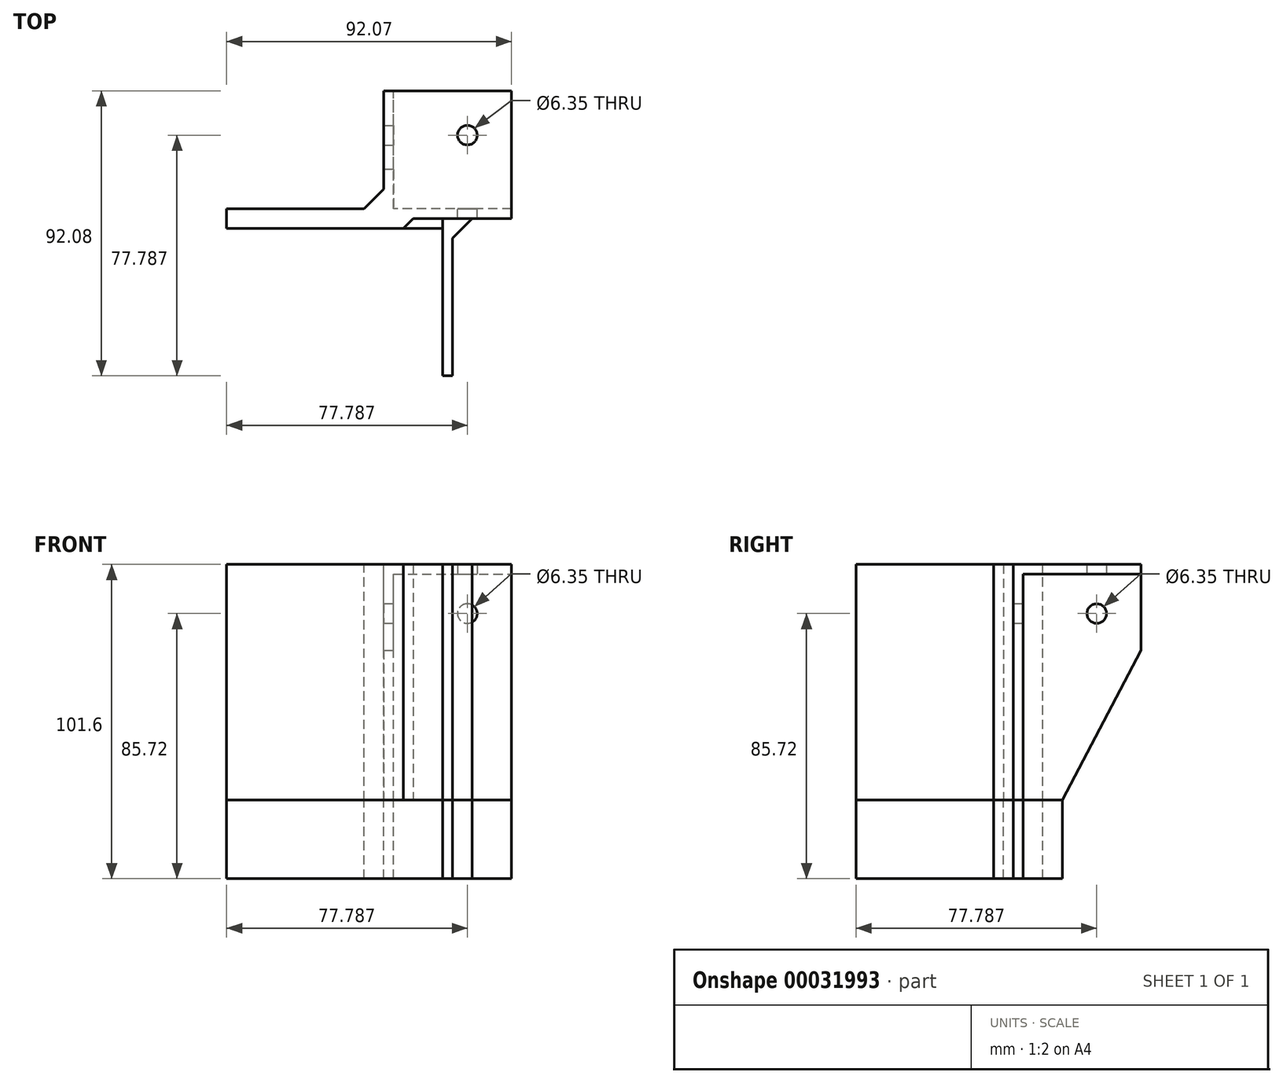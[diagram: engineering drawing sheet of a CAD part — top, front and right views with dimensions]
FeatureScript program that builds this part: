
annotation { "Feature Type Name" : "Feature", "Feature Type Description" : "" }
export const myFeature = defineFeature(function(context is Context, id is Id, definition is map)
    precondition{}
    {
        {
            var Q0;
            Q0=qCreatedBy(makeId("Top.planeOp"),FACE);
            var sketch = newSketch(context, id + "F0", { "sketchPlane" : qUnion([Q0])});
            skLineSegment(sketch, "E0.bottom", {"start": v(0, 0) * mm, "end": v(50.8, 0) * mm});
            skLineSegment(sketch, "E0.top", {"start": v(0, 50.8) * mm, "end": v(50.8, 50.8) * mm});
            skLineSegment(sketch, "E0.left", {"start": v(0, 0) * mm, "end": v(0, 50.8) * mm});
            skLineSegment(sketch, "E0.right", {"start": v(50.8, 0) * mm, "end": v(50.8, 50.8) * mm});
            skSolve(sketch);
        }
        {
            var Q0;
            Q0=makeQuery(id+"F0.imprint","IMPRINT",FACE,{"disambiguationData":[TD([[makeQuery(id+"F0.imprint","IMPRINT",EDGE,{"derivedFrom":sQuery(id+"F0.wireOp",EDGE,"E0.bottom")}),1.0]])]});
            extrude(context, id + "F1", {"entities" : qUnion([Q0]), "depth" : 3.17 * mm});
        }
        {
            var Q0;
            Q0=makeQuery(id+"F1.opExtrude","CAP_FACE",FACE,{"disambiguationData":[OSD([sQuery(id+"F0.wireOp",EDGE,"E0.bottom"),sQuery(id+"F0.wireOp",EDGE,"E0.top"),sQuery(id+"F0.wireOp",EDGE,"E0.left"),sQuery(id+"F0.wireOp",EDGE,"E0.right")])],"isStart":false});
            var sketch = newSketch(context, id + "F2", { "sketchPlane" : qUnion([Q0])});
            skLineSegment(sketch, "E1.bottom", {"start": v(50.8, 0) * mm, "end": v(-50.8, 0) * mm});
            skLineSegment(sketch, "E1.top", {"start": v(50.8, 3.18) * mm, "end": v(-50.8, 3.18) * mm});
            skLineSegment(sketch, "E1.left", {"start": v(50.8, 0) * mm, "end": v(50.8, 3.18) * mm});
            skLineSegment(sketch, "E1.right", {"start": v(-50.8, 0) * mm, "end": v(-50.8, 3.18) * mm});
            skSolve(sketch);
        }
        {
            var Q0;
            {var subQ5=sQuery(id+"F2.wireOp",EDGE,"E1.right");Q0=makeQuery(id+"F2.imprint","IMPRINT",FACE,{"disambiguationData":[TD([[makeQuery(id+"F2.imprint","IMPRINT",EDGE,{"derivedFrom":subQ5}),-1.0]])]});}
            var Q1;
            {var subQ5=sQuery(id+"F2.wireOp",EDGE,"E1.left");Q1=makeQuery(id+"F2.imprint","IMPRINT",FACE,{"disambiguationData":[TD([[makeQuery(id+"F2.imprint","IMPRINT",EDGE,{"derivedFrom":subQ5}),1.0]])]});}
            extrude(context, id + "F3", {"entities" : qUnion([Q0, Q1]), "operationType" : NewBodyOperationType.ADD, "depth" : 12.7 * mm, "hasSecondDirection" : true, "secondDirectionOppositeDirection" : true, "secondDirectionDepth" : 76.2 * mm});
        }
        {
            var Q0;
            Q0=makeQuery(id+"F1.opExtrude","CAP_FACE",FACE,{"disambiguationData":[OSD([sQuery(id+"F0.wireOp",EDGE,"E0.bottom"),sQuery(id+"F0.wireOp",EDGE,"E0.top"),sQuery(id+"F0.wireOp",EDGE,"E0.left"),sQuery(id+"F0.wireOp",EDGE,"E0.right")])],"isStart":false});
            var sketch = newSketch(context, id + "F4", { "sketchPlane" : qUnion([Q0])});
            skLineSegment(sketch, "E2.bottom", {"start": v(0, 50.8) * mm, "end": v(3.18, 50.8) * mm});
            skLineSegment(sketch, "E2.top", {"start": v(0, -50.8) * mm, "end": v(3.18, -50.8) * mm});
            skLineSegment(sketch, "E2.left", {"start": v(0, 50.8) * mm, "end": v(0, -50.8) * mm});
            skLineSegment(sketch, "E2.right", {"start": v(3.18, 50.8) * mm, "end": v(3.18, -50.8) * mm});
            skSolve(sketch);
        }
        {
            var Q0;
            Q0=qSketchRegion(id+"F4",true);
            extrude(context, id + "F5", {"entities" : qUnion([Q0]), "operationType" : NewBodyOperationType.ADD, "depth" : 12.7 * mm, "hasSecondDirection" : true, "secondDirectionOppositeDirection" : true, "secondDirectionDepth" : 76.2 * mm});
        }
        {
            var Q0;
            Q0=makeQuery(id+"F5.boolean.opBoolean","MERGE",FACE,{"derivedFrom":[makeQuery(id+"F3.opExtrude","CAP_FACE",FACE,{"disambiguationData":[OSD([sQuery(id+"F2.wireOp",EDGE,"E1.bottom"),sQuery(id+"F2.wireOp",EDGE,"E1.top"),sQuery(id+"F2.wireOp",EDGE,"E1.left"),sQuery(id+"F2.wireOp",EDGE,"E1.right")])],"isStart":false}),makeQuery(id+"F5.opExtrude","CAP_FACE",FACE,{"disambiguationData":[OSD([sQuery(id+"F4.wireOp",EDGE,"E2.bottom"),sQuery(id+"F4.wireOp",EDGE,"E2.top"),sQuery(id+"F4.wireOp",EDGE,"E2.left"),sQuery(id+"F4.wireOp",EDGE,"E2.right")])],"isStart":false})]});
            var sketch = newSketch(context, id + "F6", { "sketchPlane" : qUnion([Q0])});
            skLineSegment(sketch, "E3.0", {"start": v(3.18, 50.8) * mm, "end": v(3.18, 3.18) * mm});
            skLineSegment(sketch, "E3.1", {"start": v(0, 50.8) * mm, "end": v(3.18, 50.8) * mm});
            skLineSegment(sketch, "E3.2", {"start": v(0, 50.8) * mm, "end": v(0, 3.18) * mm});
            skLineSegment(sketch, "E3.3", {"start": v(50.8, 3.18) * mm, "end": v(3.18, 3.18) * mm});
            skLineSegment(sketch, "E3.4", {"start": v(50.8, 0) * mm, "end": v(3.18, 0) * mm});
            skLineSegment(sketch, "E3.5", {"start": v(50.8, 0) * mm, "end": v(50.8, 3.18) * mm});
            skLineSegment(sketch, "E4", {"start": v(3.18, 0) * mm, "end": v(0, 0) * mm});
            skLineSegment(sketch, "E5", {"start": v(0, 0) * mm, "end": v(0, 3.18) * mm});
            skSolve(sketch);
        }
        {
            var Q0;
            {var subQ0=sQuery(id+"F4.wireOp",EDGE,"E2.right");var subQ3=sQuery(id+"F0.wireOp",EDGE,"E0.top");Q0=makeQuery(id+"F5.boolean.opBoolean","SPLIT",FACE,{"disambiguationData":[TD([makeQuery(id+"F1.opExtrude","CAP_FACE",FACE,{"disambiguationData":[OSD([sQuery(id+"F0.wireOp",EDGE,"E0.bottom"),subQ3,sQuery(id+"F0.wireOp",EDGE,"E0.left"),sQuery(id+"F0.wireOp",EDGE,"E0.right")])],"isStart":false})])],"derivedFrom":makeQuery(id+"F5.opExtrude","SWEPT_FACE",FACE,{"disambiguationData":[OSD([subQ0])]})});}
            var sketch = newSketch(context, id + "F7", { "sketchPlane" : qUnion([Q0])});
            skLineSegment(sketch, "E6.0", {"start": v(50.8, 15.88) * mm, "end": v(50.8, 3.18) * mm});
            skLineSegment(sketch, "E6.1", {"start": v(3.18, 3.18) * mm, "end": v(50.8, 3.18) * mm});
            skLineSegment(sketch, "E6.2", {"start": v(50.8, 15.88) * mm, "end": v(3.18, 15.88) * mm});
            skLineSegment(sketch, "E6.3", {"start": v(3.18, 3.18) * mm, "end": v(3.18, 15.88) * mm});
            skSolve(sketch);
        }
        {
            var Q0;
            Q0=makeQuery(id+"F7.imprint","IMPRINT",FACE,{"disambiguationData":[TD([[makeQuery(id+"F7.imprint","IMPRINT",EDGE,{"derivedFrom":sQuery(id+"F7.wireOp",EDGE,"E6.0")}),-1.0]])]});
            extrude(context, id + "F8", {"entities" : qUnion([Q0]), "operationType" : NewBodyOperationType.REMOVE, "oppositeDirection" : true, "depth" : 25.4 * mm});
        }
        {
            var Q0;
            {var subQ0=sQuery(id+"F2.wireOp",EDGE,"E1.top");var subQ1=makeQuery(id+"F3.opExtrude","SWEPT_FACE",FACE,{"disambiguationData":[OSD([subQ0])]});var subQ11=sQuery(id+"F0.wireOp",EDGE,"E0.left");var subQ12=sQuery(id+"F0.wireOp",EDGE,"E0.right");Q0=makeQuery(id+"F8.boolean.opBoolean","MERGE",FACE,{"derivedFrom":[makeQuery(id+"F5.boolean.opBoolean","SPLIT",FACE,{"disambiguationData":[TD([makeQuery(id+"F1.opExtrude","SWEPT_FACE",FACE,{"disambiguationData":[OSD([subQ11])]})])],"derivedFrom":subQ1}),makeQuery(id+"F5.boolean.opBoolean","SPLIT",FACE,{"disambiguationData":[TD([makeQuery(id+"F1.opExtrude","CAP_FACE",FACE,{"disambiguationData":[OSD([sQuery(id+"F0.wireOp",EDGE,"E0.bottom"),sQuery(id+"F0.wireOp",EDGE,"E0.top"),subQ11,subQ12])],"isStart":false})])],"derivedFrom":subQ1}),makeQuery(id+"F8.opExtrude","SWEPT_FACE",FACE,{"disambiguationData":[OSD([sQuery(id+"F7.wireOp",EDGE,"E6.3")])]})]});}
            var sketch = newSketch(context, id + "F9", { "sketchPlane" : qUnion([Q0])});
            skLineSegment(sketch, "E7.0", {"start": v(-50.8, 15.88) * mm, "end": v(-3.18, 15.88) * mm});
            skLineSegment(sketch, "E7.1", {"start": v(-3.18, 3.18) * mm, "end": v(-50.8, 3.18) * mm});
            skLineSegment(sketch, "E7.2", {"start": v(-50.8, 15.88) * mm, "end": v(-50.8, 3.18) * mm});
            skLineSegment(sketch, "E8", {"start": v(-3.18, 15.88) * mm, "end": v(-3.18, 3.18) * mm});
            skPoint(sketch, "E9.orphan", {"position": v(0, 3.18) * mm});
            skSolve(sketch);
        }
        {
            var Q0;
            Q0=makeQuery(id+"F9.imprint","IMPRINT",FACE,{"disambiguationData":[TD([[makeQuery(id+"F9.imprint","IMPRINT",EDGE,{"derivedFrom":sQuery(id+"F9.wireOp",EDGE,"E7.0")}),-1.0]])]});
            extrude(context, id + "F10", {"entities" : qUnion([Q0]), "operationType" : NewBodyOperationType.REMOVE, "oppositeDirection" : true, "depth" : 25.4 * mm});
        }
        {
            var Q0;
            {var subQ0=sQuery(id+"F2.wireOp",EDGE,"E1.bottom");Q0=makeQuery(id+"F5.boolean.opBoolean","SPLIT",FACE,{"disambiguationData":[TD([makeQuery(id+"F1.opExtrude","SWEPT_FACE",FACE,{"disambiguationData":[OSD([sQuery(id+"F0.wireOp",EDGE,"E0.right")])]})])],"derivedFrom":makeQuery(id+"F3.boolean.opBoolean","MERGE",FACE,{"derivedFrom":[makeQuery(id+"F1.opExtrude","SWEPT_FACE",FACE,{"disambiguationData":[OSD([sQuery(id+"F0.wireOp",EDGE,"E0.bottom")])]}),makeQuery(id+"F3.opExtrude","SWEPT_FACE",FACE,{"disambiguationData":[OSD([subQ0])]})]})});}
            var sketch = newSketch(context, id + "F11", { "sketchPlane" : qUnion([Q0])});
            skLineSegment(sketch, "E10", {"start": v(3.18, -73.03) * mm, "end": v(41.28, -73.03) * mm, "construction": true});
            skLineSegment(sketch, "E11", {"start": v(50.8, 0) * mm, "end": v(50.8, -6.35) * mm, "construction": true});
            skLineSegment(sketch, "E12", {"start": v(41.28, -73.03) * mm, "end": v(50.8, -6.35) * mm});
            skLineSegment(sketch, "E13", {"start": v(50.8, -6.35) * mm, "end": v(50.8, -73.03) * mm});
            skLineSegment(sketch, "E14", {"start": v(50.8, -73.03) * mm, "end": v(41.28, -73.03) * mm});
            skSolve(sketch);
        }
        {
            var Q0;
            Q0=makeQuery(id+"F11.imprint","IMPRINT",FACE,{"disambiguationData":[TD([[makeQuery(id+"F11.imprint","IMPRINT",EDGE,{"derivedFrom":sQuery(id+"F11.wireOp",EDGE,"E12")}),-1.0]])]});
            extrude(context, id + "F12", {"entities" : qUnion([Q0]), "operationType" : NewBodyOperationType.REMOVE, "oppositeDirection" : true, "depth" : 25.4 * mm});
        }
        {
            var Q0;
            Q0=makeQuery(id+"F5.boolean.opBoolean","MERGE",FACE,{"derivedFrom":[makeQuery(id+"F1.opExtrude","SWEPT_FACE",FACE,{"disambiguationData":[OSD([sQuery(id+"F0.wireOp",EDGE,"E0.left")])]}),makeQuery(id+"F5.opExtrude","SWEPT_FACE",FACE,{"disambiguationData":[OSD([sQuery(id+"F4.wireOp",EDGE,"E2.left")])]})]});
            var sketch = newSketch(context, id + "F13", { "sketchPlane" : qUnion([Q0])});
            skLineSegment(sketch, "E15", {"start": v(-50.8, 3.18) * mm, "end": v(-50.8, -6.35) * mm, "construction": true});
            skLineSegment(sketch, "E16", {"start": v(-50.8, -6.35) * mm, "end": v(-15.88, -73.03) * mm});
            skLineSegment(sketch, "E17", {"start": v(-15.88, -73.03) * mm, "end": v(-3.18, -73.03) * mm, "construction": true});
            skLineSegment(sketch, "E18", {"start": v(-50.8, -6.35) * mm, "end": v(-50.8, -73.03) * mm});
            skLineSegment(sketch, "E19", {"start": v(-50.8, -73.03) * mm, "end": v(-15.88, -73.03) * mm});
            skSolve(sketch);
        }
        {
            var Q0;
            Q0=makeQuery(id+"F13.imprint","IMPRINT",FACE,{"disambiguationData":[TD([[makeQuery(id+"F13.imprint","IMPRINT",EDGE,{"derivedFrom":sQuery(id+"F13.wireOp",EDGE,"E16")}),-1.0]])]});
            extrude(context, id + "F14", {"entities" : qUnion([Q0]), "operationType" : NewBodyOperationType.REMOVE, "oppositeDirection" : true, "depth" : 25.4 * mm});
        }
        {
            var Q0;
            {var subQ0=sQuery(id+"F2.wireOp",EDGE,"E1.top");var subQ1=makeQuery(id+"F3.opExtrude","SWEPT_FACE",FACE,{"disambiguationData":[OSD([subQ0])]});var subQ11=sQuery(id+"F0.wireOp",EDGE,"E0.left");var subQ12=sQuery(id+"F0.wireOp",EDGE,"E0.right");Q0=makeQuery(id+"F8.boolean.opBoolean","MERGE",FACE,{"derivedFrom":[makeQuery(id+"F5.boolean.opBoolean","SPLIT",FACE,{"disambiguationData":[TD([makeQuery(id+"F1.opExtrude","SWEPT_FACE",FACE,{"disambiguationData":[OSD([subQ11])]})])],"derivedFrom":subQ1}),makeQuery(id+"F5.boolean.opBoolean","SPLIT",FACE,{"disambiguationData":[TD([makeQuery(id+"F1.opExtrude","CAP_FACE",FACE,{"disambiguationData":[OSD([sQuery(id+"F0.wireOp",EDGE,"E0.bottom"),sQuery(id+"F0.wireOp",EDGE,"E0.top"),subQ11,subQ12])],"isStart":false})])],"derivedFrom":subQ1}),makeQuery(id+"F8.opExtrude","SWEPT_FACE",FACE,{"disambiguationData":[OSD([sQuery(id+"F7.wireOp",EDGE,"E6.3")])]})]});}
            var sketch = newSketch(context, id + "F15", { "sketchPlane" : qUnion([Q0])});
            skLineSegment(sketch, "E20.bottom", {"start": v(-3.18, 15.88) * mm, "end": v(50.8, 15.88) * mm});
            skLineSegment(sketch, "E20.top", {"start": v(-3.18, 3.18) * mm, "end": v(50.8, 3.18) * mm});
            skLineSegment(sketch, "E20.left", {"start": v(-3.18, 15.88) * mm, "end": v(-3.18, 3.18) * mm});
            skLineSegment(sketch, "E20.right", {"start": v(50.8, 15.88) * mm, "end": v(50.8, 3.18) * mm});
            skSolve(sketch);
        }
        {
            var Q0;
            Q0=makeQuery(id+"F15.imprint","IMPRINT",FACE,{"disambiguationData":[TD([[makeQuery(id+"F15.imprint","IMPRINT",EDGE,{"derivedFrom":sQuery(id+"F15.wireOp",EDGE,"E20.bottom")}),-1.0]])]});
            extrude(context, id + "F16", {"entities" : qUnion([Q0]), "operationType" : NewBodyOperationType.REMOVE, "endBound" : BoundingType.THROUGH_ALL, "oppositeDirection" : true, "depth" : 25.4 * mm});
        }
        {
            var Q0;
            Q0=makeQuery(id+"F16.boolean.opBoolean","MERGE",FACE,{"derivedFrom":[makeQuery(id+"F10.boolean.opBoolean","MERGE",FACE,{"derivedFrom":[makeQuery(id+"F8.boolean.opBoolean","MERGE",FACE,{"derivedFrom":[makeQuery(id+"F1.opExtrude","CAP_FACE",FACE,{"disambiguationData":[OSD([sQuery(id+"F0.wireOp",EDGE,"E0.bottom"),sQuery(id+"F0.wireOp",EDGE,"E0.top"),sQuery(id+"F0.wireOp",EDGE,"E0.left"),sQuery(id+"F0.wireOp",EDGE,"E0.right")])],"isStart":false}),makeQuery(id+"F8.opExtrude","SWEPT_FACE",FACE,{"disambiguationData":[OSD([sQuery(id+"F7.wireOp",EDGE,"E6.1")])]})]}),makeQuery(id+"F10.opExtrude","SWEPT_FACE",FACE,{"disambiguationData":[OSD([sQuery(id+"F9.wireOp",EDGE,"E7.1")])]})]}),makeQuery(id+"F16.opExtrude","SWEPT_FACE",FACE,{"disambiguationData":[OSD([sQuery(id+"F15.wireOp",EDGE,"E20.top")])]})]});
            var sketch = newSketch(context, id + "F17", { "sketchPlane" : qUnion([Q0])});
            skLineSegment(sketch, "E21", {"start": v(3.18, 0) * mm, "end": v(3.18, -6.35) * mm});
            skLineSegment(sketch, "E22", {"start": v(3.18, -6.35) * mm, "end": v(9.53, 0) * mm});
            skLineSegment(sketch, "E23", {"start": v(9.53, 0) * mm, "end": v(3.18, 0) * mm});
            skLineSegment(sketch, "E24", {"start": v(0, 3.18) * mm, "end": v(0, 9.53) * mm});
            skLineSegment(sketch, "E25", {"start": v(0, 9.53) * mm, "end": v(-6.35, 3.18) * mm});
            skLineSegment(sketch, "E26", {"start": v(-6.35, 3.18) * mm, "end": v(0, 3.18) * mm});
            skSolve(sketch);
        }
        {
            var Q0;
            Q0=qSketchRegion(id+"F17",true);
            var Q1;
            Q1=makeQuery(id+"F5.boolean.opBoolean","MERGE",FACE,{"derivedFrom":[makeQuery(id+"F3.opExtrude","CAP_FACE",FACE,{"disambiguationData":[OSD([sQuery(id+"F2.wireOp",EDGE,"E1.bottom"),sQuery(id+"F2.wireOp",EDGE,"E1.top"),sQuery(id+"F2.wireOp",EDGE,"E1.left"),sQuery(id+"F2.wireOp",EDGE,"E1.right")])],"isStart":true}),makeQuery(id+"F5.opExtrude","CAP_FACE",FACE,{"disambiguationData":[OSD([sQuery(id+"F4.wireOp",EDGE,"E2.bottom"),sQuery(id+"F4.wireOp",EDGE,"E2.top"),sQuery(id+"F4.wireOp",EDGE,"E2.left"),sQuery(id+"F4.wireOp",EDGE,"E2.right")])],"isStart":true})]});
            extrude(context, id + "F18", {"entities" : qUnion([Q0]), "operationType" : NewBodyOperationType.ADD, "endBound" : BoundingType.UP_TO_SURFACE, "oppositeDirection" : true, "endBoundEntityFace" : qUnion([Q1]), "depth" : 25.4 * mm});
        }
        {
            var Q0;
            {var subQ0=sQuery(id+"F2.wireOp",EDGE,"E1.top");var subQ3=sQuery(id+"F0.wireOp",EDGE,"E0.right");Q0=makeQuery(id+"F5.boolean.opBoolean","SPLIT",FACE,{"disambiguationData":[TD([makeQuery(id+"F1.opExtrude","CAP_FACE",FACE,{"disambiguationData":[OSD([sQuery(id+"F0.wireOp",EDGE,"E0.bottom"),sQuery(id+"F0.wireOp",EDGE,"E0.top"),sQuery(id+"F0.wireOp",EDGE,"E0.left"),subQ3])],"isStart":true})])],"derivedFrom":makeQuery(id+"F3.opExtrude","SWEPT_FACE",FACE,{"disambiguationData":[OSD([subQ0])]})});}
            var sketch = newSketch(context, id + "F19", { "sketchPlane" : qUnion([Q0])});
            skLineSegment(sketch, "E27", {"start": v(-26.99, 0) * mm, "end": v(-26.99, -12.7) * mm, "construction": true});
            skPoint(sketch, "E27.endSnap0", {"position": v(-26.99, 0) * mm});
            skCircle(sketch, "E28", {"center": v(-26.99, -12.7) * mm, "radius": 3.18 * mm});
            skSolve(sketch);
        }
        {
            var Q0;
            Q0=qSketchRegion(id+"F19",true);
            extrude(context, id + "F20", {"entities" : qUnion([Q0]), "operationType" : NewBodyOperationType.REMOVE, "oppositeDirection" : true, "depth" : 25.4 * mm});
        }
        {
            var Q0;
            {var subQ0=sQuery(id+"F4.wireOp",EDGE,"E2.right");var subQ3=sQuery(id+"F0.wireOp",EDGE,"E0.top");Q0=makeQuery(id+"F5.boolean.opBoolean","SPLIT",FACE,{"disambiguationData":[TD([makeQuery(id+"F1.opExtrude","CAP_FACE",FACE,{"disambiguationData":[OSD([sQuery(id+"F0.wireOp",EDGE,"E0.bottom"),subQ3,sQuery(id+"F0.wireOp",EDGE,"E0.left"),sQuery(id+"F0.wireOp",EDGE,"E0.right")])],"isStart":true})])],"derivedFrom":makeQuery(id+"F5.opExtrude","SWEPT_FACE",FACE,{"disambiguationData":[OSD([subQ0])]})});}
            var sketch = newSketch(context, id + "F21", { "sketchPlane" : qUnion([Q0])});
            skLineSegment(sketch, "E29", {"start": v(26.99, 0) * mm, "end": v(26.99, -12.7) * mm, "construction": true});
            skPoint(sketch, "E29.endSnap0", {"position": v(26.99, 0) * mm});
            skCircle(sketch, "E30", {"center": v(26.99, -12.7) * mm, "radius": 3.18 * mm});
            skSolve(sketch);
        }
        {
            var Q0;
            Q0=makeQuery(id+"F21.imprint","IMPRINT",FACE,{"disambiguationData":[TD([[makeQuery(id+"F21.imprint","IMPRINT",EDGE,{"derivedFrom":sQuery(id+"F21.wireOp",EDGE,"E30")}),1.0]])]});
            extrude(context, id + "F22", {"entities" : qUnion([Q0]), "operationType" : NewBodyOperationType.REMOVE, "oppositeDirection" : true, "depth" : 25.4 * mm});
        }
        {
            var Q0;
            Q0=makeQuery(id+"F1.opExtrude","CAP_FACE",FACE,{"disambiguationData":[OSD([sQuery(id+"F0.wireOp",EDGE,"E0.bottom"),sQuery(id+"F0.wireOp",EDGE,"E0.top"),sQuery(id+"F0.wireOp",EDGE,"E0.left"),sQuery(id+"F0.wireOp",EDGE,"E0.right")])],"isStart":true});
            var sketch = newSketch(context, id + "F23", { "sketchPlane" : qUnion([Q0])});
            skLineSegment(sketch, "E31", {"start": v(3.18, -3.18) * mm, "end": v(50.8, -50.8) * mm, "construction": true});
            skLineSegment(sketch, "E32", {"start": v(50.8, -50.8) * mm, "end": v(50.8, -3.18) * mm, "construction": true});
            skLineSegment(sketch, "E33", {"start": v(50.8, -3.18) * mm, "end": v(3.17, -50.8) * mm, "construction": true});
            skCircle(sketch, "E34", {"center": v(26.99, -26.99) * mm, "radius": 3.18 * mm});
            skPoint(sketch, "E34.centerSnap0", {"position": v(26.99, -26.99) * mm});
            skSolve(sketch);
        }
        {
            var Q0;
            Q0=makeQuery(id+"F23.imprint","IMPRINT",FACE,{"disambiguationData":[TD([[makeQuery(id+"F23.imprint","IMPRINT",EDGE,{"derivedFrom":sQuery(id+"F23.wireOp",EDGE,"E34")}),1.0]])]});
            var Q1;
            Q1=sQuery(id+"F23.wireOp",EDGE,"E34");
            extrude(context, id + "F24", {"entities" : qUnion([Q0]), "operationType" : NewBodyOperationType.REMOVE, "surfaceEntities" : qUnion([Q1]), "oppositeDirection" : true, "depth" : 25.4 * mm});
        }
        {
            var Q0;
            Q0=makeQuery(id+"F18.boolean.opBoolean","MERGE",FACE,{"derivedFrom":[makeQuery(id+"F16.boolean.opBoolean","MERGE",FACE,{"derivedFrom":[makeQuery(id+"F10.boolean.opBoolean","MERGE",FACE,{"derivedFrom":[makeQuery(id+"F8.boolean.opBoolean","MERGE",FACE,{"derivedFrom":[makeQuery(id+"F1.opExtrude","CAP_FACE",FACE,{"disambiguationData":[OSD([sQuery(id+"F0.wireOp",EDGE,"E0.bottom"),sQuery(id+"F0.wireOp",EDGE,"E0.top"),sQuery(id+"F0.wireOp",EDGE,"E0.left"),sQuery(id+"F0.wireOp",EDGE,"E0.right")])],"isStart":false}),makeQuery(id+"F8.opExtrude","SWEPT_FACE",FACE,{"disambiguationData":[OSD([sQuery(id+"F7.wireOp",EDGE,"E6.1")])]})]}),makeQuery(id+"F10.opExtrude","SWEPT_FACE",FACE,{"disambiguationData":[OSD([sQuery(id+"F9.wireOp",EDGE,"E7.1")])]})]}),makeQuery(id+"F16.opExtrude","SWEPT_FACE",FACE,{"disambiguationData":[OSD([sQuery(id+"F15.wireOp",EDGE,"E20.top")])]})]}),makeQuery(id+"F18.opExtrude","CAP_FACE",FACE,{"disambiguationData":[OSD([sQuery(id+"F17.wireOp",EDGE,"E21"),sQuery(id+"F17.wireOp",EDGE,"E22"),sQuery(id+"F17.wireOp",EDGE,"E23")])],"isStart":true}),makeQuery(id+"F18.opExtrude","CAP_FACE",FACE,{"disambiguationData":[OSD([sQuery(id+"F17.wireOp",EDGE,"E24"),sQuery(id+"F17.wireOp",EDGE,"E25"),sQuery(id+"F17.wireOp",EDGE,"E26")])],"isStart":true})]});
            var sketch = newSketch(context, id + "F25", { "sketchPlane" : qUnion([Q0])});
            skLineSegment(sketch, "E35.bottom", {"start": v(50.8, 0) * mm, "end": v(41.28, 0) * mm});
            skLineSegment(sketch, "E35.top", {"start": v(50.8, 50.8) * mm, "end": v(41.27, 50.8) * mm});
            skLineSegment(sketch, "E35.left", {"start": v(50.8, 0) * mm, "end": v(50.8, 50.8) * mm});
            skLineSegment(sketch, "E35.right", {"start": v(41.28, 0) * mm, "end": v(41.27, 41.28) * mm});
            skLineSegment(sketch, "E36.bottom", {"start": v(41.27, 50.8) * mm, "end": v(0, 50.8) * mm});
            skLineSegment(sketch, "E36.top", {"start": v(41.27, 41.28) * mm, "end": v(0, 41.28) * mm});
            skLineSegment(sketch, "E36.right", {"start": v(0, 50.8) * mm, "end": v(0, 41.28) * mm});
            skSolve(sketch);
        }
        {
            var Q0;
            Q0=makeQuery(id+"F25.imprint","IMPRINT",FACE,{"disambiguationData":[TD([[makeQuery(id+"F25.imprint","IMPRINT",EDGE,{"derivedFrom":sQuery(id+"F25.wireOp",EDGE,"E35.bottom")}),1.0]])]});
            extrude(context, id + "F26", {"entities" : qUnion([Q0]), "operationType" : NewBodyOperationType.REMOVE, "endBound" : BoundingType.THROUGH_ALL, "oppositeDirection" : true, "depth" : 25.4 * mm});
        }
        {
            var Q0;
            {var subQ0=sQuery(id+"F2.wireOp",EDGE,"E1.bottom");var subQ5=sQuery(id+"F2.wireOp",EDGE,"E1.right");Q0=makeQuery(id+"F5.boolean.opBoolean","SPLIT",FACE,{"disambiguationData":[TD([makeQuery(id+"F3.opExtrude","SWEPT_FACE",FACE,{"disambiguationData":[OSD([subQ5])]})])],"derivedFrom":makeQuery(id+"F3.boolean.opBoolean","MERGE",FACE,{"derivedFrom":[makeQuery(id+"F1.opExtrude","SWEPT_FACE",FACE,{"disambiguationData":[OSD([sQuery(id+"F0.wireOp",EDGE,"E0.bottom")])]}),makeQuery(id+"F3.opExtrude","SWEPT_FACE",FACE,{"disambiguationData":[OSD([subQ0])]})]})});}
            extrude(context, id + "F27", {"entities" : qUnion([Q0]), "operationType" : NewBodyOperationType.ADD, "depth" : 3.17 * mm});
        }
        {
            var Q0;
            {var subQ0=sQuery(id+"F0.wireOp",EDGE,"E0.bottom");var subQ1=sQuery(id+"F15.wireOp",EDGE,"E20.top");Q0=makeQuery(id+"F27.boolean.opBoolean","MERGE",FACE,{"derivedFrom":[makeQuery(id+"F18.boolean.opBoolean","MERGE",FACE,{"derivedFrom":[makeQuery(id+"F16.boolean.opBoolean","MERGE",FACE,{"derivedFrom":[makeQuery(id+"F10.boolean.opBoolean","MERGE",FACE,{"derivedFrom":[makeQuery(id+"F8.boolean.opBoolean","MERGE",FACE,{"derivedFrom":[makeQuery(id+"F1.opExtrude","CAP_FACE",FACE,{"disambiguationData":[OSD([subQ0,sQuery(id+"F0.wireOp",EDGE,"E0.top"),sQuery(id+"F0.wireOp",EDGE,"E0.left"),sQuery(id+"F0.wireOp",EDGE,"E0.right")])],"isStart":false}),makeQuery(id+"F8.opExtrude","SWEPT_FACE",FACE,{"disambiguationData":[OSD([sQuery(id+"F7.wireOp",EDGE,"E6.1")])]})]}),makeQuery(id+"F10.opExtrude","SWEPT_FACE",FACE,{"disambiguationData":[OSD([sQuery(id+"F9.wireOp",EDGE,"E7.1")])]})]}),makeQuery(id+"F16.opExtrude","SWEPT_FACE",FACE,{"disambiguationData":[OSD([subQ1])]})]}),makeQuery(id+"F18.opExtrude","CAP_FACE",FACE,{"disambiguationData":[OSD([sQuery(id+"F17.wireOp",EDGE,"E21"),sQuery(id+"F17.wireOp",EDGE,"E22"),sQuery(id+"F17.wireOp",EDGE,"E23")])],"isStart":true}),makeQuery(id+"F18.opExtrude","CAP_FACE",FACE,{"disambiguationData":[OSD([sQuery(id+"F17.wireOp",EDGE,"E24"),sQuery(id+"F17.wireOp",EDGE,"E25"),sQuery(id+"F17.wireOp",EDGE,"E26")])],"isStart":true})]}),makeQuery(id+"F27.opExtrude","SWEPT_FACE",FACE,{"disambiguationData":[OSD([subQ0,sQuery(id+"F2.wireOp",EDGE,"E1.bottom"),subQ1])]})]});}
            var sketch = newSketch(context, id + "F28", { "sketchPlane" : qUnion([Q0])});
            skLineSegment(sketch, "E37", {"start": v(3.18, -12.1) * mm, "end": v(22.23, -12.1) * mm, "construction": true});
            skPoint(sketch, "E38.oppositeSnap0", {"position": v(1.59, -50.8) * mm});
            skLineSegment(sketch, "E38.bottom", {"start": v(22.23, 0) * mm, "end": v(19.05, 0) * mm});
            skLineSegment(sketch, "E38.top", {"start": v(22.23, -50.8) * mm, "end": v(19.05, -50.8) * mm});
            skLineSegment(sketch, "E38.left", {"start": v(22.23, -6.35) * mm, "end": v(22.23, -50.8) * mm});
            skLineSegment(sketch, "E38.right", {"start": v(19.05, 0) * mm, "end": v(19.05, -50.8) * mm});
            skLineSegment(sketch, "E39", {"start": v(22.23, 0) * mm, "end": v(28.57, 0) * mm});
            skLineSegment(sketch, "E40", {"start": v(28.57, 0) * mm, "end": v(22.23, -6.35) * mm});
            skSolve(sketch);
        }
        {
            var Q0;
            Q0=makeQuery(id+"F28.imprint","IMPRINT",FACE,{"disambiguationData":[TD([[makeQuery(id+"F28.imprint","IMPRINT",EDGE,{"derivedFrom":sQuery(id+"F28.wireOp",EDGE,"E38.bottom")}),-1.0]])]});
            var Q1;
            {var subQ0=sQuery(id+"F2.wireOp",EDGE,"E1.bottom");Q1=makeQuery(id+"F27.boolean.opBoolean","MERGE",FACE,{"derivedFrom":[makeQuery(id+"F18.boolean.opBoolean","MERGE",FACE,{"derivedFrom":[makeQuery(id+"F5.boolean.opBoolean","MERGE",FACE,{"derivedFrom":[makeQuery(id+"F3.opExtrude","CAP_FACE",FACE,{"disambiguationData":[OSD([subQ0,sQuery(id+"F2.wireOp",EDGE,"E1.top"),sQuery(id+"F2.wireOp",EDGE,"E1.left"),sQuery(id+"F2.wireOp",EDGE,"E1.right")])],"isStart":true}),makeQuery(id+"F5.opExtrude","CAP_FACE",FACE,{"disambiguationData":[OSD([sQuery(id+"F4.wireOp",EDGE,"E2.bottom"),sQuery(id+"F4.wireOp",EDGE,"E2.top"),sQuery(id+"F4.wireOp",EDGE,"E2.left"),sQuery(id+"F4.wireOp",EDGE,"E2.right")])],"isStart":true})]}),makeQuery(id+"F18.opExtrude","CAP_FACE",FACE,{"disambiguationData":[OSD([sQuery(id+"F17.wireOp",EDGE,"E21"),sQuery(id+"F17.wireOp",EDGE,"E22"),sQuery(id+"F17.wireOp",EDGE,"E23")])],"isStart":false}),makeQuery(id+"F18.opExtrude","CAP_FACE",FACE,{"disambiguationData":[OSD([sQuery(id+"F17.wireOp",EDGE,"E24"),sQuery(id+"F17.wireOp",EDGE,"E25"),sQuery(id+"F17.wireOp",EDGE,"E26")])],"isStart":false})]}),makeQuery(id+"F27.opExtrude","SWEPT_FACE",FACE,{"disambiguationData":[OSD([subQ0])]})]});}
            extrude(context, id + "F29", {"entities" : qUnion([Q0]), "endBound" : BoundingType.UP_TO_SURFACE, "oppositeDirection" : true, "endBoundEntityFace" : qUnion([Q1]), "depth" : 25.4 * mm});
        }
        {
            var Q0;
            {var subQ0=sQuery(id+"F0.wireOp",EDGE,"E0.bottom");var subQ1=sQuery(id+"F15.wireOp",EDGE,"E20.top");Q0=makeQuery(id+"F27.boolean.opBoolean","MERGE",FACE,{"derivedFrom":[makeQuery(id+"F18.boolean.opBoolean","MERGE",FACE,{"derivedFrom":[makeQuery(id+"F16.boolean.opBoolean","MERGE",FACE,{"derivedFrom":[makeQuery(id+"F10.boolean.opBoolean","MERGE",FACE,{"derivedFrom":[makeQuery(id+"F8.boolean.opBoolean","MERGE",FACE,{"derivedFrom":[makeQuery(id+"F1.opExtrude","CAP_FACE",FACE,{"disambiguationData":[OSD([subQ0,sQuery(id+"F0.wireOp",EDGE,"E0.top"),sQuery(id+"F0.wireOp",EDGE,"E0.left"),sQuery(id+"F0.wireOp",EDGE,"E0.right")])],"isStart":false}),makeQuery(id+"F8.opExtrude","SWEPT_FACE",FACE,{"disambiguationData":[OSD([sQuery(id+"F7.wireOp",EDGE,"E6.1")])]})]}),makeQuery(id+"F10.opExtrude","SWEPT_FACE",FACE,{"disambiguationData":[OSD([sQuery(id+"F9.wireOp",EDGE,"E7.1")])]})]}),makeQuery(id+"F16.opExtrude","SWEPT_FACE",FACE,{"disambiguationData":[OSD([subQ1])]})]}),makeQuery(id+"F18.opExtrude","CAP_FACE",FACE,{"disambiguationData":[OSD([sQuery(id+"F17.wireOp",EDGE,"E21"),sQuery(id+"F17.wireOp",EDGE,"E22"),sQuery(id+"F17.wireOp",EDGE,"E23")])],"isStart":true}),makeQuery(id+"F18.opExtrude","CAP_FACE",FACE,{"disambiguationData":[OSD([sQuery(id+"F17.wireOp",EDGE,"E24"),sQuery(id+"F17.wireOp",EDGE,"E25"),sQuery(id+"F17.wireOp",EDGE,"E26")])],"isStart":true})]}),makeQuery(id+"F27.opExtrude","SWEPT_FACE",FACE,{"disambiguationData":[OSD([subQ0,sQuery(id+"F2.wireOp",EDGE,"E1.bottom"),subQ1])]})]});}
            var sketch = newSketch(context, id + "F30", { "sketchPlane" : qUnion([Q0])});
            skLineSegment(sketch, "E41.0", {"start": v(3.18, -50.8) * mm, "end": v(3.18, -6.35) * mm});
            skLineSegment(sketch, "E41.1", {"start": v(3.17, -6.35) * mm, "end": v(6.35, -3.18) * mm});
            skLineSegment(sketch, "E41.2", {"start": v(0, -3.18) * mm, "end": v(0, -50.8) * mm});
            skLineSegment(sketch, "E41.3", {"start": v(0, -50.8) * mm, "end": v(3.18, -50.8) * mm});
            skLineSegment(sketch, "E42", {"start": v(0, -3.18) * mm, "end": v(6.35, -3.18) * mm});
            skPoint(sketch, "E43.orphan", {"position": v(9.53, 0) * mm});
            skSolve(sketch);
        }
        {
            var Q0;
            Q0=makeQuery(id+"F30.imprint","IMPRINT",FACE,{"disambiguationData":[TD([[makeQuery(id+"F30.imprint","IMPRINT",EDGE,{"derivedFrom":sQuery(id+"F30.wireOp",EDGE,"E41.0")}),1.0]])]});
            extrude(context, id + "F31", {"entities" : qUnion([Q0]), "operationType" : NewBodyOperationType.REMOVE, "endBound" : BoundingType.THROUGH_ALL, "oppositeDirection" : true, "depth" : 25.4 * mm});
        }
        {
            var Q0;
            Q0=makeQuery(id+"F29.opExtrude","SWEPT_FACE",FACE,{"disambiguationData":[OSD([sQuery(id+"F28.wireOp",EDGE,"E38.right")])]});
            var sketch = newSketch(context, id + "F32", { "sketchPlane" : qUnion([Q0])});
            skLineSegment(sketch, "E44.0", {"start": v(3.18, -73.02) * mm, "end": v(3.18, 3.18) * mm});
            skLineSegment(sketch, "E44.1", {"start": v(3.18, 3.18) * mm, "end": v(0, 3.18) * mm});
            skLineSegment(sketch, "E44.2", {"start": v(0, -73.02) * mm, "end": v(0, 3.17) * mm});
            skLineSegment(sketch, "E44.3", {"start": v(0, -73.02) * mm, "end": v(3.18, -73.02) * mm});
            skSolve(sketch);
        }
        {
            var Q0;
            Q0 = qSketchRegion(id + "F32", true);
            extrude(context, id + "F33", {"entities" : qUnion([Q0]), "endBound" : BoundingType.UP_TO_NEXT, "depth" : 25.4 * mm});
        }
        {
            var Q0;
            {var subQ0=sQuery(id+"F2.wireOp",EDGE,"E1.bottom");Q0=makeQuery(id+"F27.boolean.opBoolean","MERGE",FACE,{"derivedFrom":[makeQuery(id+"F18.boolean.opBoolean","MERGE",FACE,{"derivedFrom":[makeQuery(id+"F5.boolean.opBoolean","MERGE",FACE,{"derivedFrom":[makeQuery(id+"F3.opExtrude","CAP_FACE",FACE,{"disambiguationData":[OSD([subQ0,sQuery(id+"F2.wireOp",EDGE,"E1.top"),sQuery(id+"F2.wireOp",EDGE,"E1.left"),sQuery(id+"F2.wireOp",EDGE,"E1.right")])],"isStart":true}),makeQuery(id+"F5.opExtrude","CAP_FACE",FACE,{"disambiguationData":[OSD([sQuery(id+"F4.wireOp",EDGE,"E2.bottom"),sQuery(id+"F4.wireOp",EDGE,"E2.top"),sQuery(id+"F4.wireOp",EDGE,"E2.left"),sQuery(id+"F4.wireOp",EDGE,"E2.right")])],"isStart":true})]}),makeQuery(id+"F18.opExtrude","CAP_FACE",FACE,{"disambiguationData":[OSD([sQuery(id+"F17.wireOp",EDGE,"E21"),sQuery(id+"F17.wireOp",EDGE,"E22"),sQuery(id+"F17.wireOp",EDGE,"E23")])],"isStart":false}),makeQuery(id+"F18.opExtrude","CAP_FACE",FACE,{"disambiguationData":[OSD([sQuery(id+"F17.wireOp",EDGE,"E24"),sQuery(id+"F17.wireOp",EDGE,"E25"),sQuery(id+"F17.wireOp",EDGE,"E26")])],"isStart":false})]}),makeQuery(id+"F27.opExtrude","SWEPT_FACE",FACE,{"disambiguationData":[OSD([subQ0])]})]});}
            var sketch = newSketch(context, id + "F34", { "sketchPlane" : qUnion([Q0])});
            skLineSegment(sketch, "E45.0", {"start": v(6.35, 3.18) * mm, "end": v(-50.8, 3.18) * mm});
            skLineSegment(sketch, "E45.1", {"start": v(-50.8, 3.18) * mm, "end": v(-50.8, -3.18) * mm});
            skLineSegment(sketch, "E45.2", {"start": v(-6.35, -3.18) * mm, "end": v(-50.8, -3.18) * mm});
            skLineSegment(sketch, "E45.3", {"start": v(-6.35, -3.18) * mm, "end": v(0, -9.53) * mm});
            skLineSegment(sketch, "E45.4", {"start": v(0, -15.88) * mm, "end": v(0, -9.53) * mm});
            skLineSegment(sketch, "E45.5", {"start": v(3.18, -15.88) * mm, "end": v(0, -15.88) * mm});
            skLineSegment(sketch, "E45.6", {"start": v(3.18, -15.88) * mm, "end": v(3.18, -3.18) * mm});
            skLineSegment(sketch, "E45.7", {"start": v(41.28, -3.18) * mm, "end": v(3.18, -3.18) * mm});
            skLineSegment(sketch, "E45.8", {"start": v(41.28, -3.18) * mm, "end": v(41.28, 0) * mm});
            skLineSegment(sketch, "E45.9", {"start": v(41.27, 0) * mm, "end": v(28.57, 0) * mm});
            skLineSegment(sketch, "E45.10", {"start": v(22.23, 6.35) * mm, "end": v(28.57, 0) * mm});
            skLineSegment(sketch, "E45.11", {"start": v(22.23, 50.8) * mm, "end": v(22.23, 6.35) * mm});
            skLineSegment(sketch, "E45.12", {"start": v(19.05, 50.8) * mm, "end": v(19.05, 3.18) * mm});
            skLineSegment(sketch, "E45.13", {"start": v(19.05, 50.8) * mm, "end": v(22.23, 50.8) * mm});
            skLineSegment(sketch, "E45.14", {"start": v(6.35, 3.18) * mm, "end": v(19.05, 3.18) * mm});
            skPoint(sketch, "E46.orphan", {"position": v(9.53, 0) * mm});
            skPoint(sketch, "E47.orphan", {"position": v(19.05, 0) * mm});
            skSolve(sketch);
        }
        {
            var Q0;
            Q0 = qSketchRegion(id + "F34", true);
            extrude(context, id + "F35", {"entities" : qUnion([Q0]), "depth" : 25.4 * mm});
        }
    });
